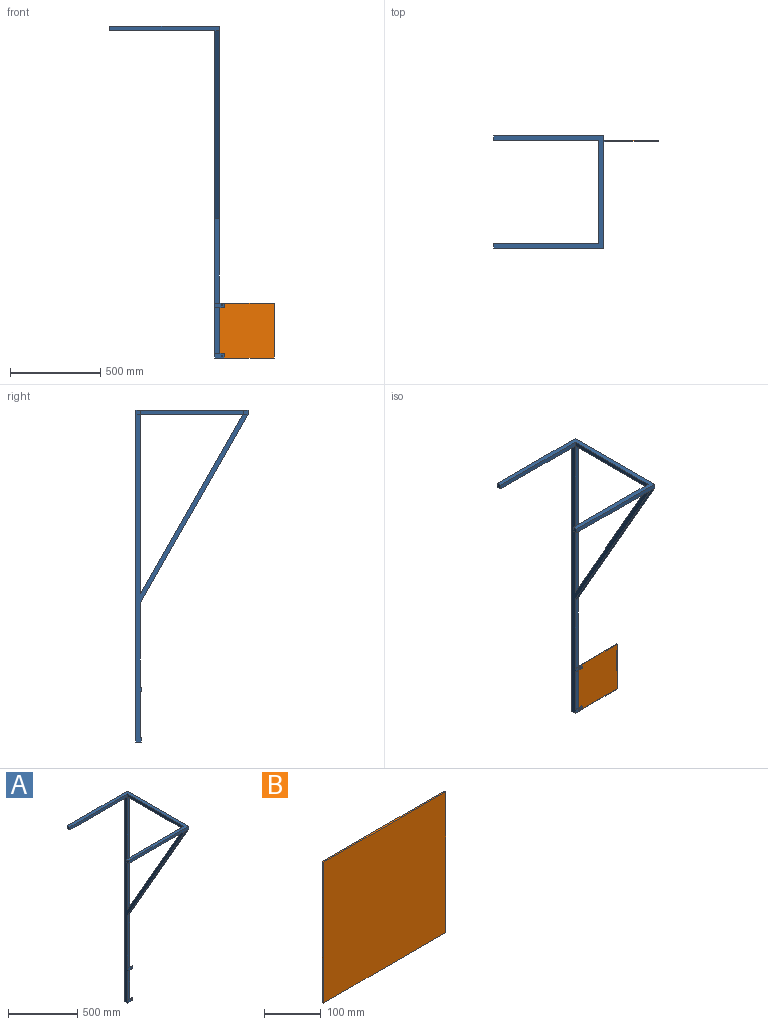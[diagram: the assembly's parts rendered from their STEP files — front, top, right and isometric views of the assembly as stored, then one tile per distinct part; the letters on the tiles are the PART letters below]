
ASSEMBLY  parts=2 mates=1
PART A: 29 faces, bbox 635x622.3x1841.5 mm
  f0: plane 466.73x25.4mm, normal (0,-1,0), area 11854.8mm2, adj f2,f9,f11,f24
  f1: plane 254x25.4mm, normal (0,-1,0), area 6451.6mm2, adj f2,f9,f18,f25
  f2: plane 1841.5x622.3mm, normal (-1,0,0), area 90616mm2, adj f0,f1,f4,f5,f6,f7,f8,f10
  f3: plane 609.6x25.4mm, normal (0,-1,0), area 15483.8mm2, adj f5,f9,f11,f15,f17
  f4: plane 50.8x28.58mm, normal (0,0,-1), area 806.4mm2, adj f2,f8,f9,f19,f21,f22
  f5: plane 622.3x609.6mm, normal (0,0,1), area 45483.8mm2, adj f2,f3,f8,f9,f13,f14,f16,f17
  f6: plane 567.65x25.4mm, normal (0,0,-1), area 14418.2mm2, adj f2,f7,f9,f10
  f7: plane 993.38x25.4mm, normal (0,-1,0), area 25231.8mm2, adj f2,f6,f9,f10
  f8: plane 1841.5x609.6mm, normal (0,1,0), area 61612.8mm2, adj f2,f4,f5,f9,f12,f14
  f9: plane 1841.5x622.3mm, normal (1,0,0), area 91745mm2, adj f0,f1,f3,f4,f5,f6,f7,f8
  f10: plane 993.38x567.65mm, normal (0,0.87,0.5), area 29060.8mm2, adj f2,f6,f7,f9
  f11: plane 1044.58x596.9mm, normal (0,-0.87,-0.5), area 30558.5mm2, adj f0,f2,f3,f9
  f12: plane 584.2x25.4mm, normal (0,0,-1), area 14838.7mm2, adj f2,f8,f13,f14
  f13: plane 584.2x25.4mm, normal (0,-1,0), area 14838.7mm2, adj f2,f5,f12,f14
  f14: plane 25.4x25.4mm, normal (-1,0,0), area 645.2mm2, adj f5,f8,f12,f13
  f15: plane 584.2x25.4mm, normal (0,0,-1), area 14838.7mm2, adj f2,f3,f16,f17
  f16: plane 584.2x25.4mm, normal (0,1,0), area 14838.7mm2, adj f2,f5,f15,f17
  f17: plane 25.4x25.4mm, normal (-1,0,0), area 645.2mm2, adj f3,f5,f15,f16
  f18: plane 50.8x3.18mm, normal (0,0,1), area 161.3mm2, adj f1,f2,f19,f21,f22
  f19: plane 25.4x3.18mm, normal (1,0,0), area 80.6mm2, adj f4,f18,f21,f22
  f20: cylinder r=3.17mm len=6.35mm, axis (0,1,0), area 63.3mm2, adj f21,f22
  f21: plane 50.8x25.4mm, normal (0,-1,0), area 1258.7mm2, adj f2,f4,f18,f19,f20
  f22: plane 25.4x25.4mm, normal (0,1,0), area 613.5mm2, adj f4,f9,f18,f19,f20
  f23: plane 25.4x25.4mm, normal (0,1,0), area 613.5mm2, adj f9,f24,f25,f26,f27
  f24: plane 50.8x3.18mm, normal (0,0,1), area 161.3mm2, adj f0,f2,f23,f26,f28
  f25: plane 50.8x3.18mm, normal (0,0,-1), area 161.3mm2, adj f1,f2,f23,f26,f28
  f26: plane 25.4x3.18mm, normal (1,0,0), area 80.6mm2, adj f23,f24,f25,f28
  f27: cylinder r=3.17mm len=6.35mm, axis (0,1,0), area 63.3mm2, adj f23,f28
  f28: plane 50.8x25.4mm, normal (0,-1,0), area 1258.7mm2, adj f2,f24,f25,f26,f27
PART B: 6 faces, bbox 304.8x3.2x304.8 mm
  f0: plane 304.8x3.18mm, normal (-1,0,0), area 967.7mm2, adj f1,f3,f4,f5
  f1: plane 304.8x3.18mm, normal (0,0,-1), area 967.7mm2, adj f0,f2,f4,f5
  f2: plane 304.8x3.18mm, normal (1,0,0), area 967.7mm2, adj f1,f3,f4,f5
  f3: plane 304.8x3.18mm, normal (0,0,1), area 967.7mm2, adj f0,f2,f4,f5
  f4: plane 304.8x304.8mm, normal (0,1,0), area 92903mm2, adj f0,f1,f2,f3
  f5: plane 304.8x304.8mm, normal (0,-1,0), area 92903mm2, adj f0,f1,f2,f3
PLACE A at identity fixed
PLACE B at identity
MATE fastened A.f0 <-> B.f5  axis (0,1,0) through (12.7,-12.7,-1524)mm
